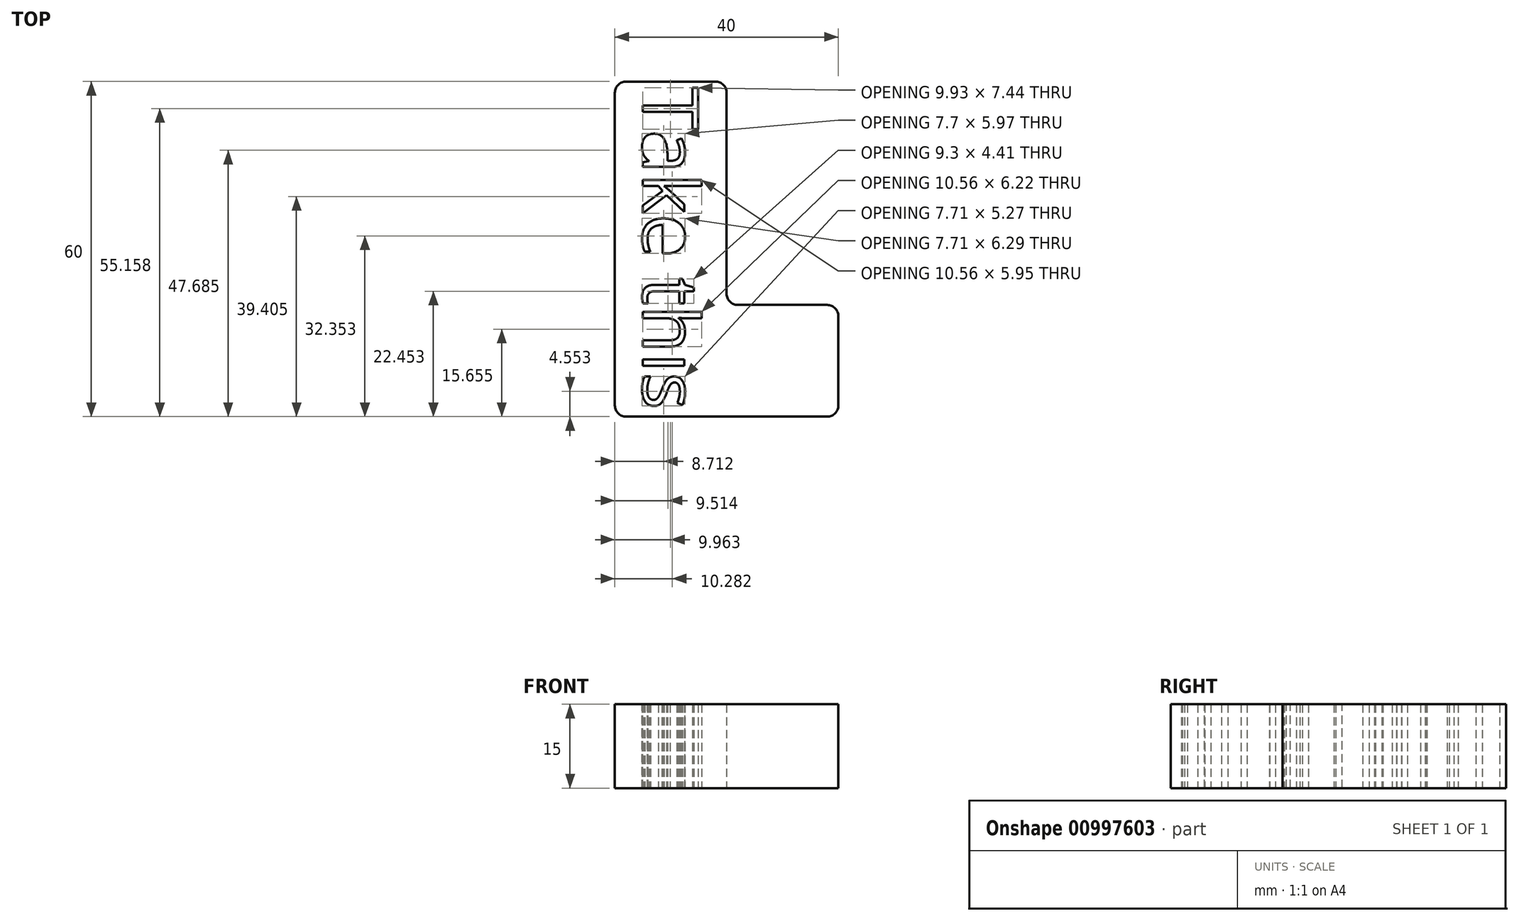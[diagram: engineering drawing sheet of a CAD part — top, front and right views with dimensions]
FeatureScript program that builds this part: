
annotation { "Feature Type Name" : "Feature", "Feature Type Description" : "" }
export const myFeature = defineFeature(function(context is Context, id is Id, definition is map)
    precondition{}
    {
        {
            var Q0;
            Q0=qCreatedBy(makeId("Top.planeOp"),FACE);
            var sketch = newSketch(context, id + "F0", { "sketchPlane" : qUnion([Q0])});
            skLineSegment(sketch, "E0", {"start": v(-60.35, 82.76) * mm, "end": v(-60.35, 22.76) * mm});
            skLineSegment(sketch, "E1", {"start": v(-60.35, 22.76) * mm, "end": v(-20.35, 22.76) * mm});
            skLineSegment(sketch, "E2", {"start": v(-20.35, 22.76) * mm, "end": v(-20.35, 42.76) * mm});
            skLineSegment(sketch, "E3", {"start": v(-20.35, 42.76) * mm, "end": v(-40.35, 42.76) * mm});
            skLineSegment(sketch, "E4", {"start": v(-40.35, 42.76) * mm, "end": v(-40.35, 82.76) * mm});
            skLineSegment(sketch, "E5", {"start": v(-40.35, 82.76) * mm, "end": v(-60.35, 82.76) * mm});
            skText(sketch, "E6", { "text": "Take this", "fontName": "OpenSans-Regular.ttf"});
            skPoint(sketch, "E7", {"position": v(-50.35, 81.76) * mm});
            skPoint(sketch, "E7.positionSnap0", {"position": v(-50.35, 82.76) * mm});
            const initialGuessF0  = {"E6": [-0.05535, 0.08176, 0, -1, 0.01001]};
            skSetInitialGuess(sketch, initialGuessF0);
            skSolve(sketch);
        }
        {
            var Q0;
            Q0 = qSketchRegion(id + "F0", true);
            var Q1;
            Q1=makeQuery(id+"F0.imprint","IMPRINT",FACE,{"disambiguationData":[TD([[makeQuery(id+"F0.imprint","IMPRINT",EDGE,{"derivedFrom":sQuery(id+"F0.wireOp",EDGE,"E6.sketch_text.stroke-110")}),-1.0]])]});
            extrude(context, id + "F1", {"entities" : qUnion([Q0, Q1]), "depth" : 15 * mm, "offsetDistance" : 25 * mm});
        }
        {
            var Q0;
            Q0=makeQuery(id+"F1.opExtrude","SWEPT_EDGE",EDGE,{"disambiguationData":[OSD([sQuery(id+"F0.wireOp",EDGE,"E2"),sQuery(id+"F0.wireOp",EDGE,"E3")])]});
            var Q1;
            Q1=makeQuery(id+"F1.opExtrude","SWEPT_EDGE",EDGE,{"disambiguationData":[OSD([sQuery(id+"F0.wireOp",EDGE,"E1"),sQuery(id+"F0.wireOp",EDGE,"E2")])]});
            var Q2;
            Q2=makeQuery(id+"F1.opExtrude","SWEPT_EDGE",EDGE,{"disambiguationData":[OSD([sQuery(id+"F0.wireOp",EDGE,"E3"),sQuery(id+"F0.wireOp",EDGE,"E4")])]});
            var Q3;
            Q3=makeQuery(id+"F1.opExtrude","SWEPT_EDGE",EDGE,{"disambiguationData":[OSD([sQuery(id+"F0.wireOp",EDGE,"E4"),sQuery(id+"F0.wireOp",EDGE,"E5")])]});
            var Q4;
            Q4=makeQuery(id+"F1.opExtrude","SWEPT_EDGE",EDGE,{"disambiguationData":[OSD([sQuery(id+"F0.wireOp",EDGE,"E0"),sQuery(id+"F0.wireOp",EDGE,"E5")])]});
            var Q5;
            Q5=makeQuery(id+"F1.opExtrude","SWEPT_EDGE",EDGE,{"disambiguationData":[OSD([sQuery(id+"F0.wireOp",EDGE,"E0"),sQuery(id+"F0.wireOp",EDGE,"E1")])]});
            fillet(context, id + "F2", {"entities" : qUnion([Q0, Q1, Q2, Q3, Q4, Q5]), "radius" : 2 * mm, "tangentPropagation" : true, "allowEdgeOverflow" : false});
        }
    });
